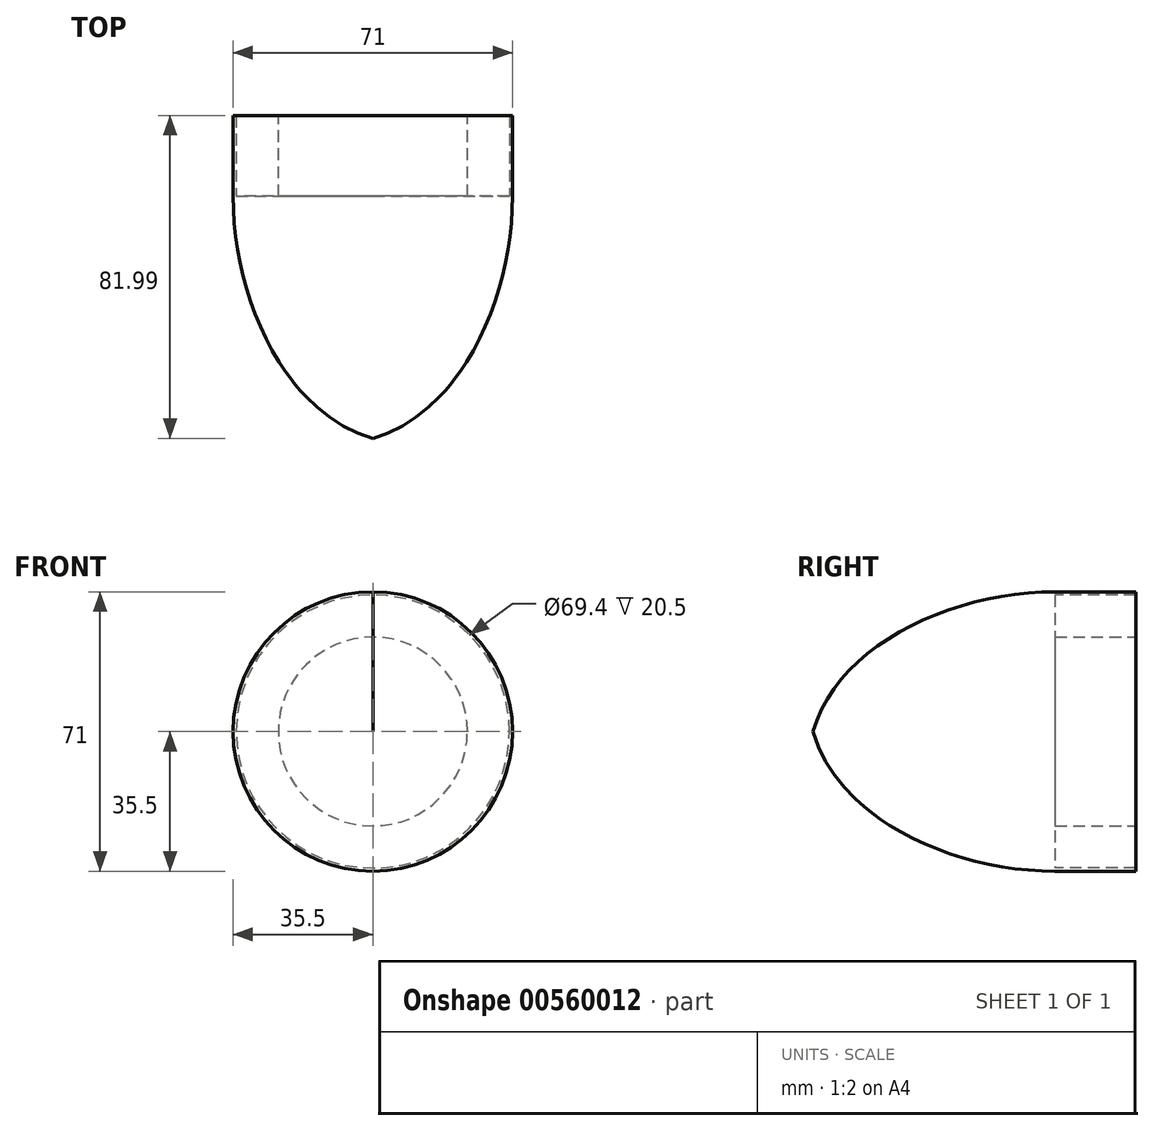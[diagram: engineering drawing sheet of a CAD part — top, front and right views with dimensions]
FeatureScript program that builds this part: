
annotation { "Feature Type Name" : "Feature", "Feature Type Description" : "" }
export const myFeature = defineFeature(function(context is Context, id is Id, definition is map)
    precondition{}
    {
        {
            var Q0;
            Q0=qCreatedBy(makeId("Right.planeOp"),FACE);
            var sketch = newSketch(context, id + "F0", { "sketchPlane" : qUnion([Q0])});
            skLineSegment(sketch, "E0", {"start": v(0, 0) * mm, "end": v(-81.99, 0) * mm});
            skLineSegment(sketch, "E1", {"start": v(0, 0) * mm, "end": v(0, 24) * mm});
            skLineSegment(sketch, "E2", {"start": v(0, 24) * mm, "end": v(-20.5, 24) * mm});
            skLineSegment(sketch, "E3", {"start": v(-20.5, 24) * mm, "end": v(-20.5, 35.5) * mm});
            skLineSegment(sketch, "E4", {"start": v(-20.5, 35.5) * mm, "end": v(-81.99, 0) * mm, "construction": true});
            skFitSpline(sketch, "E5", {"points": [v(-20.5, 35.5) * mm, v(-81.99, 0) * mm], "startDerivative": vector(-77.79, 0) * mm, "endDerivative": vector(-18.92, -66.9) * mm});
            skSolve(sketch);
        }
        {
            var Q0;
            Q0=makeQuery(id+"F0.imprint","IMPRINT",FACE,{"disambiguationData":[TD([[makeQuery(id+"F0.imprint","IMPRINT",EDGE,{"derivedFrom":sQuery(id+"F0.wireOp",EDGE,"E0")}),-1.0]])]});
            var Q1;
            Q1=sQuery(id+"F0.wireOp",EDGE,"E0");
            revolve(context, id + "F1", {"entities" : qUnion([Q0]), "axis" : qUnion([Q1]), "revolveType" : RevolveType.FULL});
        }
        {
            var Q0;
            Q0=makeQuery(id+"F1.opRevolve","SWEPT_FACE",FACE,{"disambiguationData":[OSD([sQuery(id+"F0.wireOp",EDGE,"E3")])]});
            var sketch = newSketch(context, id + "F2", { "sketchPlane" : qUnion([Q0])});
            skCircle(sketch, "E6.0", {"center": v(0, 0) * mm, "radius": 35.5 * mm});
            skCircle(sketch, "E7.0", {"center": v(0, 0) * mm, "radius": 34.7 * mm});
            skSolve(sketch);
        }
        {
            var Q0;
            Q0 = qSketchRegion(id + "F2", true);
            var Q1;
            Q1=makeQuery(id+"F1.opRevolve","SWEPT_FACE",FACE,{"disambiguationData":[OSD([sQuery(id+"F0.wireOp",EDGE,"E1")])]});
            extrude(context, id + "F3", {"entities" : qUnion([Q0]), "operationType" : NewBodyOperationType.ADD, "endBound" : BoundingType.UP_TO_SURFACE, "depth" : 25 * mm, "endBoundEntityFace" : qUnion([Q1]), "offsetDistance" : 25 * mm});
        }
    });
